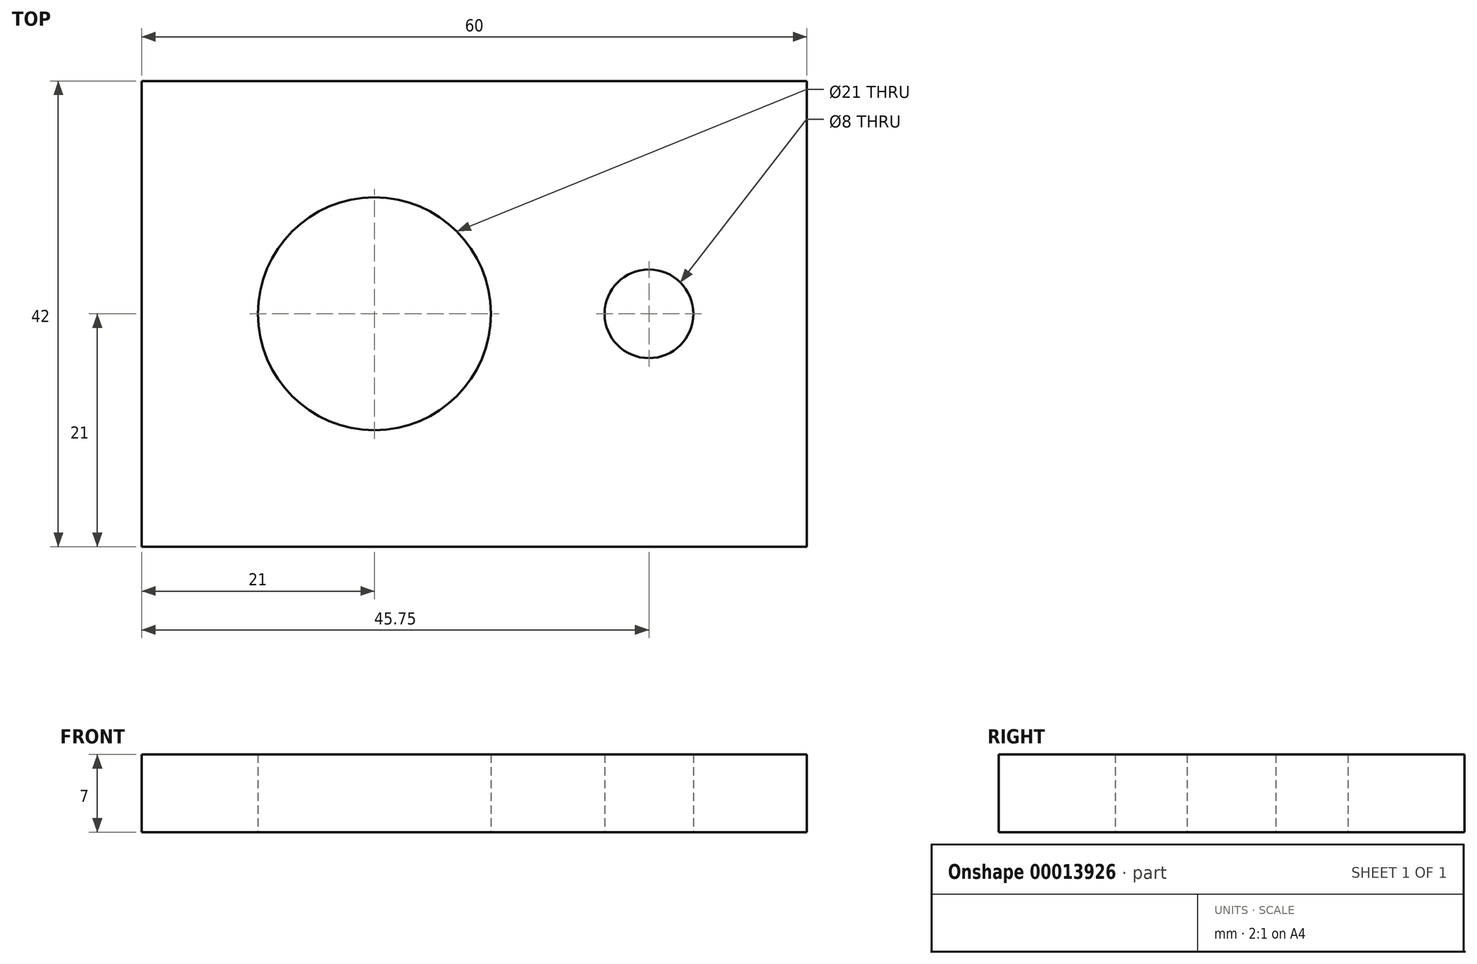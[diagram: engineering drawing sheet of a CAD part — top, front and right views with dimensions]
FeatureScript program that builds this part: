
annotation { "Feature Type Name" : "Feature", "Feature Type Description" : "" }
export const myFeature = defineFeature(function(context is Context, id is Id, definition is map)
    precondition{}
    {
        {
            var Q0;
            Q0=qCreatedBy(makeId("Top.planeOp"),FACE);
            var sketch = newSketch(context, id + "F0", { "sketchPlane" : qUnion([Q0])});
            skCircle(sketch, "E0", {"center": v(0, 0) * mm, "radius": 10.5 * mm});
            skLineSegment(sketch, "E1.bottom", {"start": v(-21, 21) * mm, "end": v(39, 21) * mm});
            skLineSegment(sketch, "E1.top", {"start": v(-21, -21) * mm, "end": v(39, -21) * mm});
            skLineSegment(sketch, "E1.left", {"start": v(-21, 21) * mm, "end": v(-21, -21) * mm});
            skLineSegment(sketch, "E1.right", {"start": v(39, 21) * mm, "end": v(39, -21) * mm});
            skCircle(sketch, "E2", {"center": v(24.75, 0) * mm, "radius": 4 * mm});
            skLineSegment(sketch, "E3", {"start": v(0, 0) * mm, "end": v(-21, 0) * mm, "construction": true});
            skPoint(sketch, "E4", {"position": v(-10.5, 0) * mm});
            skLineSegment(sketch, "E5", {"start": v(10.5, 0) * mm, "end": v(39, 0) * mm, "construction": true});
            skLineSegment(sketch, "E6", {"start": v(0, 0) * mm, "end": v(0, 21) * mm, "construction": true});
            skPoint(sketch, "E7", {"position": v(0, 10.5) * mm});
            skSolve(sketch);
        }
        {
            var Q0;
            Q0 = qSketchRegion(id + "F0", true);
            extrude(context, id + "F1", {"entities" : qUnion([Q0]), "depth" : 7 * mm});
        }
    });
